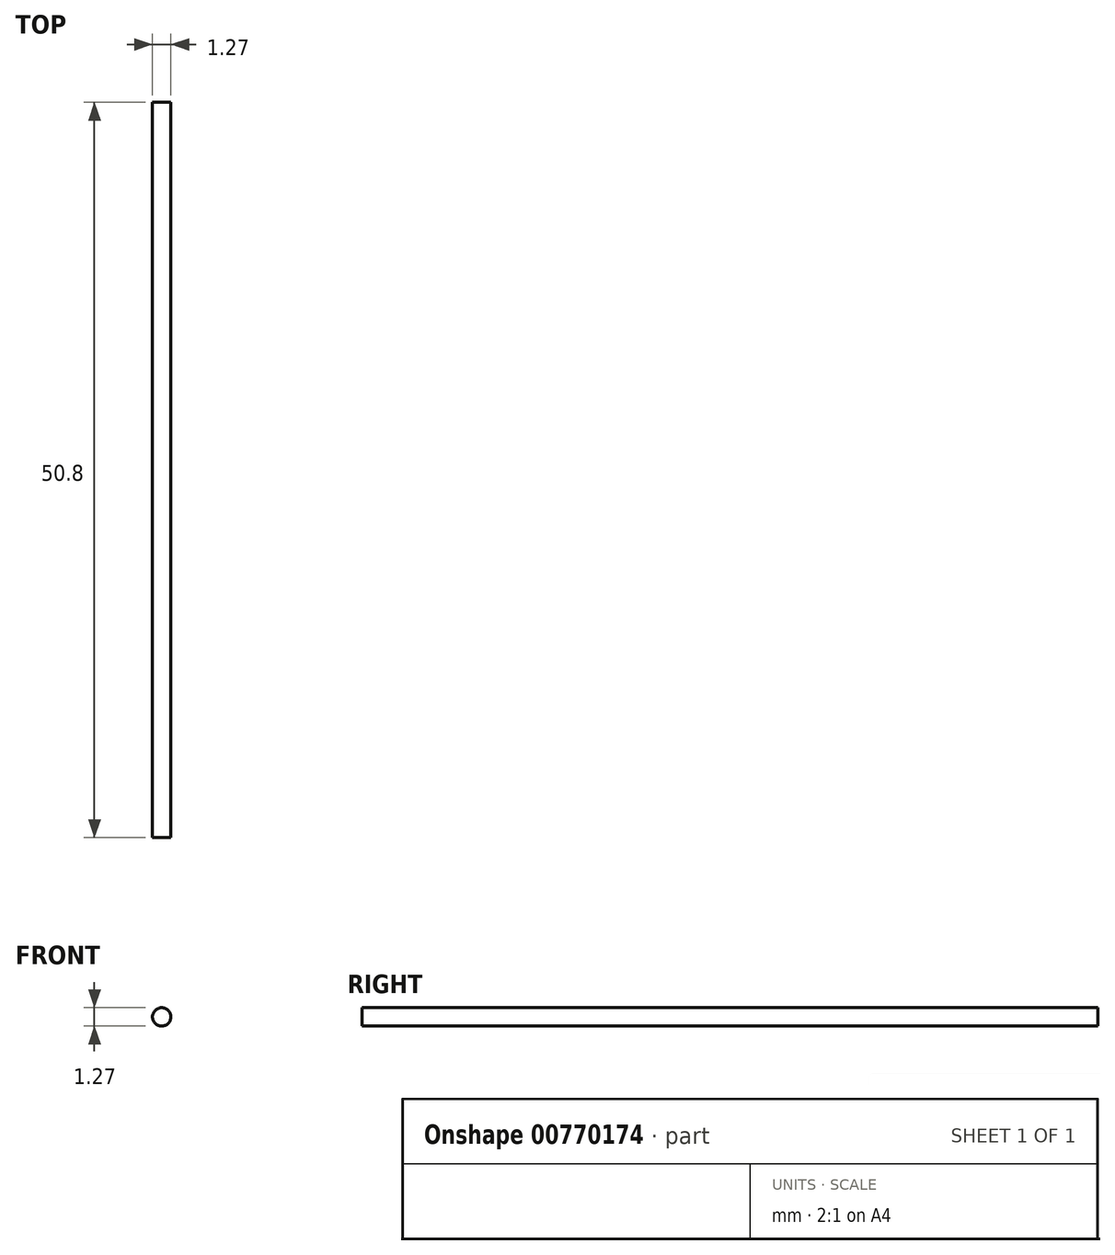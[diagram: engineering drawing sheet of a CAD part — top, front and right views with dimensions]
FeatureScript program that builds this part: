
annotation { "Feature Type Name" : "Feature", "Feature Type Description" : "" }
export const myFeature = defineFeature(function(context is Context, id is Id, definition is map)
    precondition{}
    {
        {
            var Q0;
            Q0=qCreatedBy(makeId("Front.planeOp"),FACE);
            var sketch = newSketch(context, id + "F0", { "sketchPlane" : qUnion([Q0])});
            skCircle(sketch, "E0", {"center": v(-8.01, 8.85) * mm, "radius": 0.64 * mm});
            skSolve(sketch);
        }
        {
            var Q0;
            Q0=makeQuery(id+"F0.imprint","IMPRINT",FACE,{"disambiguationData":[TD([[makeQuery(id+"F0.imprint","IMPRINT",EDGE,{"derivedFrom":sQuery(id+"F0.wireOp",EDGE,"E0")}),1.0]])]});
            var Q1;
            Q1 = qSketchRegion(id + "F0", true);
            extrude(context, id + "F1", {"entities" : qUnion([Q0, Q1]), "depth" : 50.8 * mm, "offsetDistance" : 25.4 * mm});
        }
    });
